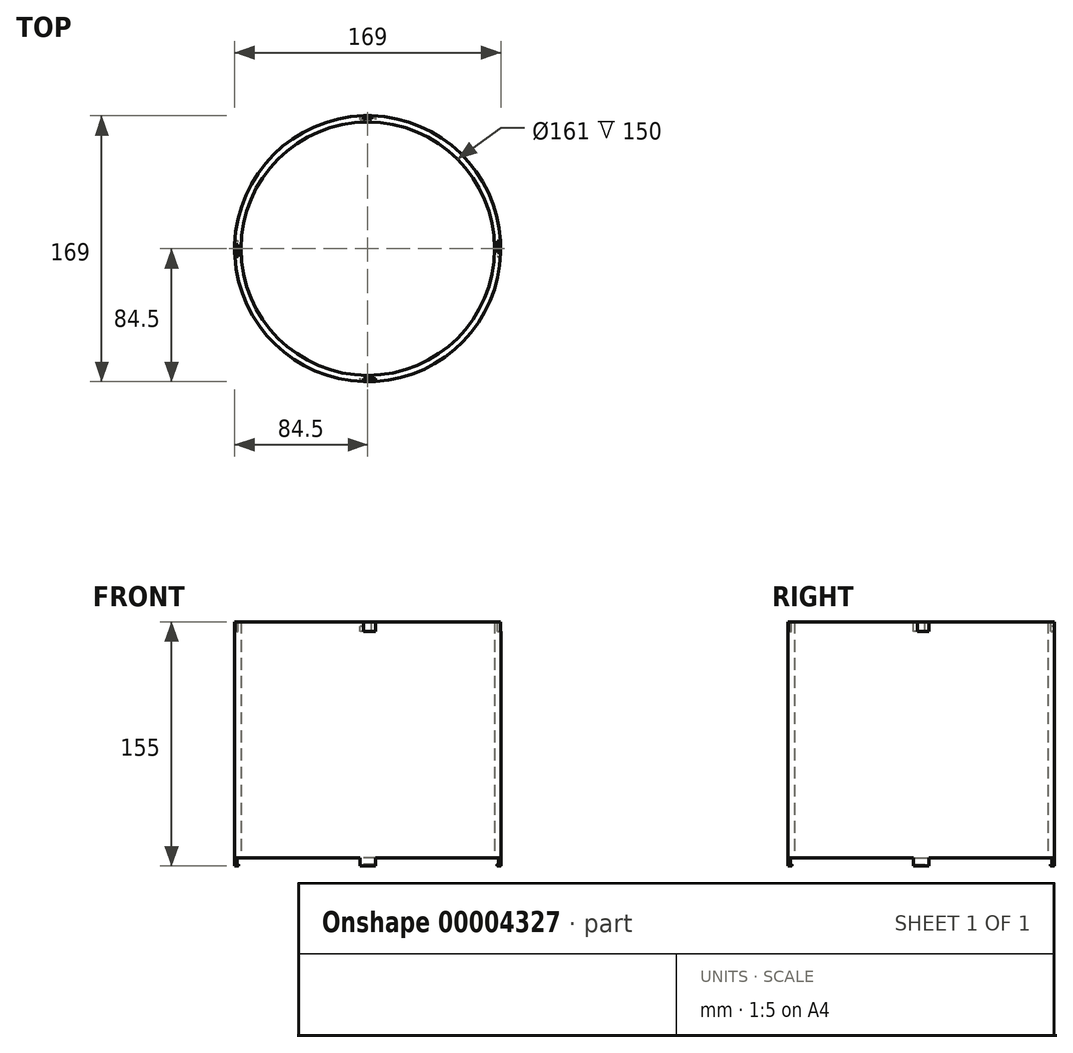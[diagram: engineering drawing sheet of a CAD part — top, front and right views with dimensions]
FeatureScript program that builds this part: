
annotation { "Feature Type Name" : "Feature", "Feature Type Description" : "" }
export const myFeature = defineFeature(function(context is Context, id is Id, definition is map)
    precondition{}
    {
        {
            var Q0;
            Q0=qCreatedBy(makeId("Top.planeOp"),FACE);
            var sketch = newSketch(context, id + "F0", { "sketchPlane" : qUnion([Q0])});
            skCircle(sketch, "E0", {"center": v(0, 0) * mm, "radius": 90 * mm});
            skSolve(sketch);
        }
        {
            var Q0;
            Q0=makeQuery(id+"F0.imprint","IMPRINT",FACE,{"disambiguationData":[TD([[makeQuery(id+"F0.imprint","IMPRINT",EDGE,{"derivedFrom":sQuery(id+"F0.wireOp",EDGE,"E0")}),1.0]])]});
            extrude(context, id + "F1", {"entities" : qUnion([Q0]), "oppositeDirection" : true, "depth" : 150 * mm});
        }
        {
            var Q0;
            Q0=makeQuery(id+"F1.opExtrude","CAP_FACE",FACE,{"disambiguationData":[OSD([sQuery(id+"F0.wireOp",EDGE,"E0")])],"isStart":true});
            var sketch = newSketch(context, id + "F2", { "sketchPlane" : qUnion([Q0])});
            skCircle(sketch, "E1.0", {"center": v(0, 0) * mm, "radius": 80 * mm});
            skSolve(sketch);
        }
        {
            var Q0;
            Q0=makeQuery(id+"F2.imprint","IMPRINT",FACE,{"disambiguationData":[TD([[makeQuery(id+"F2.imprint","IMPRINT",EDGE,{"derivedFrom":sQuery(id+"F2.wireOp",EDGE,"E1.0")}),1.0]])]});
            extrude(context, id + "F3", {"entities" : qUnion([Q0]), "operationType" : NewBodyOperationType.REMOVE, "oppositeDirection" : true, "depth" : 100 * mm});
        }
        {
            var Q0;
            Q0=makeQuery(id+"F1.opExtrude","CAP_FACE",FACE,{"disambiguationData":[OSD([sQuery(id+"F0.wireOp",EDGE,"E0")])],"isStart":true});
            var sketch = newSketch(context, id + "F4", { "sketchPlane" : qUnion([Q0])});
            skCircle(sketch, "E2.0", {"center": v(0, 0) * mm, "radius": 84.5 * mm});
            skSolve(sketch);
        }
        {
            var Q0;
            Q0=makeQuery(id+"F4.imprint","IMPRINT",FACE,{"disambiguationData":[TD([[makeQuery(id+"F4.imprint","IMPRINT",EDGE,{"derivedFrom":sQuery(id+"F4.wireOp",EDGE,"E2.0")}),-1.0]])]});
            extrude(context, id + "F5", {"entities" : qUnion([Q0]), "operationType" : NewBodyOperationType.REMOVE, "oppositeDirection" : true, "depth" : 150 * mm});
        }
        {
            var Q0;
            Q0=makeQuery(id+"F1.opExtrude","CAP_FACE",FACE,{"disambiguationData":[OSD([sQuery(id+"F0.wireOp",EDGE,"E0")])],"isStart":false});
            var sketch = newSketch(context, id + "F6", { "sketchPlane" : qUnion([Q0])});
            skCircle(sketch, "E3.0", {"center": v(0, 0) * mm, "radius": 80.5 * mm});
            skSolve(sketch);
        }
        {
            var Q0;
            Q0=makeQuery(id+"F6.imprint","IMPRINT",FACE,{"disambiguationData":[TD([[makeQuery(id+"F6.imprint","IMPRINT",EDGE,{"derivedFrom":sQuery(id+"F6.wireOp",EDGE,"E3.0")}),1.0]])]});
            extrude(context, id + "F7", {"entities" : qUnion([Q0]), "operationType" : NewBodyOperationType.REMOVE, "oppositeDirection" : true, "depth" : 179.6 * mm});
        }
        {
            var Q0;
            Q0=makeQuery(id+"F1.opExtrude","CAP_FACE",FACE,{"disambiguationData":[OSD([sQuery(id+"F0.wireOp",EDGE,"E0")])],"isStart":false});
            var sketch = newSketch(context, id + "F8", { "sketchPlane" : qUnion([Q0])});
            skLineSegment(sketch, "E4.0", {"start": v(-85, 0) * mm, "end": v(-85, 5) * mm});
            skLineSegment(sketch, "E4.1", {"start": v(-85, 0) * mm, "end": v(-85, -5) * mm});
            skLineSegment(sketch, "E5.0", {"start": v(-83, 0) * mm, "end": v(-83, -5) * mm});
            skLineSegment(sketch, "E5.1", {"start": v(-83, 0) * mm, "end": v(-83, 5) * mm});
            skLineSegment(sketch, "E6", {"start": v(-85, 5) * mm, "end": v(-82.9, 5) * mm});
            skLineSegment(sketch, "E7", {"start": v(-85, -5) * mm, "end": v(-82.9, -5) * mm});
            skLineSegment(sketch, "E8.0", {"start": v(0, -83) * mm, "end": v(5, -83) * mm});
            skLineSegment(sketch, "E8.1", {"start": v(0, -83) * mm, "end": v(-5, -83) * mm});
            skLineSegment(sketch, "E9.0", {"start": v(0, -85) * mm, "end": v(5, -85) * mm});
            skLineSegment(sketch, "E9.1", {"start": v(0, -85) * mm, "end": v(-5, -85) * mm});
            skLineSegment(sketch, "E10", {"start": v(-5, -83) * mm, "end": v(-5, -85) * mm});
            skLineSegment(sketch, "E11", {"start": v(5, -85) * mm, "end": v(5, -83) * mm});
            skLineSegment(sketch, "E12.0", {"start": v(83, 0) * mm, "end": v(83, -5) * mm});
            skLineSegment(sketch, "E12.1", {"start": v(83, 0) * mm, "end": v(83, 5) * mm});
            skLineSegment(sketch, "E13.0", {"start": v(85, 0) * mm, "end": v(85, 5) * mm});
            skLineSegment(sketch, "E13.1", {"start": v(85, 0) * mm, "end": v(85, -5) * mm});
            skLineSegment(sketch, "E14", {"start": v(83, 5) * mm, "end": v(85, 5) * mm});
            skLineSegment(sketch, "E15", {"start": v(85, -5) * mm, "end": v(83, -5) * mm});
            skLineSegment(sketch, "E16.0", {"start": v(0, 85) * mm, "end": v(-5, 85) * mm});
            skLineSegment(sketch, "E16.1", {"start": v(0, 85) * mm, "end": v(5, 85) * mm});
            skLineSegment(sketch, "E17.0", {"start": v(0, 83) * mm, "end": v(5, 83) * mm});
            skLineSegment(sketch, "E17.1", {"start": v(0, 83) * mm, "end": v(-5, 83) * mm});
            skLineSegment(sketch, "E18", {"start": v(-5, 85) * mm, "end": v(-5, 83) * mm});
            skLineSegment(sketch, "E19", {"start": v(5, 85) * mm, "end": v(5, 83) * mm});
            skCircle(sketch, "E20.0", {"center": v(0, 0) * mm, "radius": 84.5 * mm});
            skSolve(sketch);
        }
        {
            var Q0;
            {var subQ3=sQuery(id+"F8.wireOp",EDGE,"E5.0");var subQ6=sQuery(id+"F8.wireOp",EDGE,"E7");var subQ10=makeQuery(id+"F8.imprint","INTERSECT",VERTEX,{"derivedFrom":[subQ3,subQ6]});Q0=makeQuery(id+"F8.imprint","IMPRINT",FACE,{"disambiguationData":[TD([[makeQuery(id+"F8.imprint","IMPRINT",EDGE,{"disambiguationData":[TD([[subQ10,1.0]])],"derivedFrom":subQ3}),-1.0]])]});}
            var Q1;
            {var subQ3=sQuery(id+"F8.wireOp",EDGE,"E8.0");var subQ5=sQuery(id+"F8.wireOp",EDGE,"E11");var subQ8=makeQuery(id+"F8.imprint","INTERSECT",VERTEX,{"derivedFrom":[subQ3,subQ5]});Q1=makeQuery(id+"F8.imprint","IMPRINT",FACE,{"disambiguationData":[TD([[makeQuery(id+"F8.imprint","IMPRINT",EDGE,{"disambiguationData":[TD([[subQ8,1.0]])],"derivedFrom":subQ3}),-1.0]])]});}
            var Q2;
            {var subQ3=sQuery(id+"F8.wireOp",EDGE,"E12.0");var subQ6=sQuery(id+"F8.wireOp",EDGE,"E15");var subQ10=makeQuery(id+"F8.imprint","INTERSECT",VERTEX,{"derivedFrom":[subQ3,subQ6]});Q2=makeQuery(id+"F8.imprint","IMPRINT",FACE,{"disambiguationData":[TD([[makeQuery(id+"F8.imprint","IMPRINT",EDGE,{"disambiguationData":[TD([[subQ10,1.0]])],"derivedFrom":subQ3}),1.0]])]});}
            var Q3;
            {var subQ1=sQuery(id+"F8.wireOp",EDGE,"E19");var subQ5=sQuery(id+"F8.wireOp",EDGE,"E17.0");var subQ6=makeQuery(id+"F8.imprint","INTERSECT",VERTEX,{"derivedFrom":[subQ5,subQ1]});Q3=makeQuery(id+"F8.imprint","IMPRINT",FACE,{"disambiguationData":[TD([[makeQuery(id+"F8.imprint","IMPRINT",EDGE,{"disambiguationData":[TD([[subQ6,1.0]])],"derivedFrom":subQ5}),1.0]])]});}
            extrude(context, id + "F9", {"entities" : qUnion([Q0, Q1, Q2, Q3]), "operationType" : NewBodyOperationType.ADD, "depth" : 5 * mm});
        }
        {
            var Q0;
            Q0=makeQuery(id+"F9.opExtrude","SWEPT_FACE",FACE,{"disambiguationData":[OSD([sQuery(id+"F8.wireOp",EDGE,"E12.0"),sQuery(id+"F8.wireOp",EDGE,"E12.1")])]});
            var sketch = newSketch(context, id + "F10", { "sketchPlane" : qUnion([Q0])});
            skLineSegment(sketch, "E21.0", {"start": v(-5, -154) * mm, "end": v(5, -154) * mm});
            skSolve(sketch);
        }
        {
            var Q0;
            Q0=makeQuery(id+"F9.opExtrude","SWEPT_FACE",FACE,{"disambiguationData":[OSD([sQuery(id+"F8.wireOp",EDGE,"E17.0"),sQuery(id+"F8.wireOp",EDGE,"E17.1")])]});
            var sketch = newSketch(context, id + "F11", { "sketchPlane" : qUnion([Q0])});
            skLineSegment(sketch, "E22.0", {"start": v(-5, -154) * mm, "end": v(5, -154) * mm});
            skSolve(sketch);
        }
        {
            var Q0;
            Q0=makeQuery(id+"F9.opExtrude","SWEPT_FACE",FACE,{"disambiguationData":[OSD([sQuery(id+"F8.wireOp",EDGE,"E5.0"),sQuery(id+"F8.wireOp",EDGE,"E5.1")])]});
            var sketch = newSketch(context, id + "F12", { "sketchPlane" : qUnion([Q0])});
            skLineSegment(sketch, "E23.0", {"start": v(-5, -154) * mm, "end": v(5, -154) * mm});
            skSolve(sketch);
        }
        {
            var Q0;
            Q0=makeQuery(id+"F9.opExtrude","SWEPT_FACE",FACE,{"disambiguationData":[OSD([sQuery(id+"F8.wireOp",EDGE,"E8.0"),sQuery(id+"F8.wireOp",EDGE,"E8.1")])]});
            var sketch = newSketch(context, id + "F13", { "sketchPlane" : qUnion([Q0])});
            skLineSegment(sketch, "E24.0", {"start": v(-5, -154) * mm, "end": v(5, -154) * mm});
            skSolve(sketch);
        }
        {
            var Q0;
            {var subQ2=sQuery(id+"F13.wireOp",EDGE,"E24.0");Q0=makeQuery(id+"F13.imprint","IMPRINT",FACE,{"disambiguationData":[TD([[makeQuery(id+"F13.imprint","IMPRINT",EDGE,{"derivedFrom":subQ2}),-1.0]])]});}
            extrude(context, id + "F14", {"entities" : qUnion([Q0]), "operationType" : NewBodyOperationType.ADD, "depth" : 1 * mm});
        }
        {
            var Q0;
            {var subQ2=sQuery(id+"F10.wireOp",EDGE,"E21.0");Q0=makeQuery(id+"F10.imprint","IMPRINT",FACE,{"disambiguationData":[TD([[makeQuery(id+"F10.imprint","IMPRINT",EDGE,{"derivedFrom":subQ2}),-1.0]])]});}
            extrude(context, id + "F15", {"entities" : qUnion([Q0]), "operationType" : NewBodyOperationType.ADD, "depth" : 1 * mm});
        }
        {
            var Q0;
            {var subQ2=sQuery(id+"F11.wireOp",EDGE,"E22.0");Q0=makeQuery(id+"F11.imprint","IMPRINT",FACE,{"disambiguationData":[TD([[makeQuery(id+"F11.imprint","IMPRINT",EDGE,{"derivedFrom":subQ2}),-1.0]])]});}
            extrude(context, id + "F16", {"entities" : qUnion([Q0]), "operationType" : NewBodyOperationType.ADD, "depth" : 1 * mm});
        }
        {
            var Q0;
            {var subQ2=sQuery(id+"F12.wireOp",EDGE,"E23.0");Q0=makeQuery(id+"F12.imprint","IMPRINT",FACE,{"disambiguationData":[TD([[makeQuery(id+"F12.imprint","IMPRINT",EDGE,{"derivedFrom":subQ2}),-1.0]])]});}
            extrude(context, id + "F17", {"entities" : qUnion([Q0]), "operationType" : NewBodyOperationType.ADD, "depth" : 1 * mm});
        }
        {
            var Q0;
            Q0=makeQuery(id+"F17.opExtrude","CAP_EDGE",EDGE,{"disambiguationData":[OSD([sQuery(id+"F8.wireOp",EDGE,"E5.0"),sQuery(id+"F8.wireOp",EDGE,"E5.1")])],"isStart":false});
            var Q1;
            Q1=makeQuery(id+"F17.opExtrude","CAP_EDGE",EDGE,{"disambiguationData":[OSD([sQuery(id+"F12.wireOp",EDGE,"E23.0")])],"isStart":false});
            fillet(context, id + "F18", {"entities" : qUnion([Q0, Q1]), "radius" : 0.5 * mm, "tangentPropagation" : true, "allowEdgeOverflow" : false});
        }
        {
            var Q0;
            Q0=makeQuery(id+"F14.opExtrude","CAP_EDGE",EDGE,{"disambiguationData":[OSD([sQuery(id+"F13.wireOp",EDGE,"a1c1dbc0-bdf1-4701-884e-e09ee9ca7c5f.0")])],"isStart":false});
            var Q1;
            Q1=makeQuery(id+"F14.opExtrude","CAP_EDGE",EDGE,{"disambiguationData":[OSD([sQuery(id+"F8.wireOp",EDGE,"E8.0"),sQuery(id+"F8.wireOp",EDGE,"E8.1")])],"isStart":false});
            fillet(context, id + "F19", {"entities" : qUnion([Q0, Q1]), "radius" : 0.5 * mm, "tangentPropagation" : true, "allowEdgeOverflow" : false});
        }
        {
            var Q0;
            Q0=makeQuery(id+"F15.opExtrude","CAP_EDGE",EDGE,{"disambiguationData":[OSD([sQuery(id+"F8.wireOp",EDGE,"E12.0"),sQuery(id+"F8.wireOp",EDGE,"E12.1")])],"isStart":false});
            var Q1;
            Q1=makeQuery(id+"F15.opExtrude","CAP_EDGE",EDGE,{"disambiguationData":[OSD([sQuery(id+"F10.wireOp",EDGE,"E21.0")])],"isStart":false});
            fillet(context, id + "F20", {"entities" : qUnion([Q0, Q1]), "radius" : 0.5 * mm, "tangentPropagation" : true, "allowEdgeOverflow" : false});
        }
        {
            var Q0;
            Q0=makeQuery(id+"F16.opExtrude","CAP_EDGE",EDGE,{"disambiguationData":[OSD([sQuery(id+"F8.wireOp",EDGE,"E17.0"),sQuery(id+"F8.wireOp",EDGE,"E17.1")])],"isStart":false});
            var Q1;
            Q1=makeQuery(id+"F16.opExtrude","CAP_EDGE",EDGE,{"disambiguationData":[OSD([sQuery(id+"F11.wireOp",EDGE,"E22.0")])],"isStart":false});
            fillet(context, id + "F21", {"entities" : qUnion([Q0, Q1]), "radius" : 0.5 * mm, "tangentPropagation" : true, "allowEdgeOverflow" : false});
        }
        {
            var Q0;
            Q0=makeQuery(id+"F4.imprint","IMPRINT",FACE,{"disambiguationData":[TD([[makeQuery(id+"F4.imprint","IMPRINT",EDGE,{"derivedFrom":sQuery(id+"F4.wireOp",EDGE,"E2.0")}),1.0]])]});
            var sketch = newSketch(context, id + "F22", { "sketchPlane" : qUnion([Q0])});
            skCircle(sketch, "E25.0", {"center": v(0, 0) * mm, "radius": 84.5 * mm});
            skCircle(sketch, "E26.0", {"center": v(0, 0) * mm, "radius": 80 * mm});
            skLineSegment(sketch, "E27", {"start": v(-84.5, 2.5) * mm, "end": v(-81.5, 2.5) * mm});
            skLineSegment(sketch, "E28", {"start": v(-84.5, -2.5) * mm, "end": v(-84.46, -2.5) * mm});
            skLineSegment(sketch, "E29", {"start": v(2.5, 81.81) * mm, "end": v(2.5, 84.5) * mm});
            skLineSegment(sketch, "E30", {"start": v(81.3, -2.5) * mm, "end": v(84.5, -2.5) * mm});
            skLineSegment(sketch, "E31", {"start": v(-2.5, -84.5) * mm, "end": v(-2.5, -82.5) * mm});
            skLineSegment(sketch, "E32", {"start": v(-2.5, -84.5) * mm, "end": v(-2.5, -81.7) * mm});
            skLineSegment(sketch, "E33.0", {"start": v(5, -81.52) * mm, "end": v(5, -84.5) * mm});
            skLineSegment(sketch, "E34.0", {"start": v(81.4, 5) * mm, "end": v(84.5, 5) * mm});
            skLineSegment(sketch, "E35.0", {"start": v(-5, 84.5) * mm, "end": v(-5, 81.47) * mm});
            skLineSegment(sketch, "E36.0", {"start": v(-84.5, -5) * mm, "end": v(-80.8, -5) * mm});
            skCircle(sketch, "E37.0", {"center": v(0, 0) * mm, "radius": 82.5 * mm});
            skSolve(sketch);
        }
        {
            var Q0;
            {var subQ5=sQuery(id+"F22.wireOp",EDGE,"E25.0");var subQ7=makeQuery(id+"F22.imprint","IMPRINT",VERTEX,{"derivedFrom":subQ5});Q0=makeQuery(id+"F22.imprint","IMPRINT",FACE,{"disambiguationData":[TD([[makeQuery(id+"F22.imprint","IMPRINT",EDGE,{"disambiguationData":[TD([[subQ7,1.0]])],"derivedFrom":subQ5}),1.0]])]});}
            var Q1;
            {var subQ3=sQuery(id+"F22.wireOp",EDGE,"E32");var subQ8=makeQuery(id+"F22.imprint","IMPRINT",VERTEX,{"derivedFrom":subQ3});Q1=makeQuery(id+"F22.imprint","IMPRINT",FACE,{"disambiguationData":[TD([[makeQuery(id+"F22.imprint","IMPRINT",EDGE,{"disambiguationData":[TD([[subQ8,1.0]])],"derivedFrom":subQ3}),-1.0]])]});}
            var Q2;
            {var subQ3=sQuery(id+"F22.wireOp",EDGE,"E30");var subQ5=sQuery(id+"F22.wireOp",EDGE,"E25.0");var subQ7=makeQuery(id+"F22.imprint","INTERSECT",VERTEX,{"derivedFrom":[subQ3,subQ5]});Q2=makeQuery(id+"F22.imprint","IMPRINT",FACE,{"disambiguationData":[TD([[makeQuery(id+"F22.imprint","IMPRINT",EDGE,{"disambiguationData":[TD([[subQ7,1.0]])],"derivedFrom":subQ3}),1.0]])]});}
            var Q3;
            {var subQ0=sQuery(id+"F22.wireOp",EDGE,"E25.0");var subQ3=sQuery(id+"F22.wireOp",EDGE,"E29");var subQ4=makeQuery(id+"F22.imprint","INTERSECT",VERTEX,{"derivedFrom":[subQ3,subQ0]});Q3=makeQuery(id+"F22.imprint","IMPRINT",FACE,{"disambiguationData":[TD([[makeQuery(id+"F22.imprint","IMPRINT",EDGE,{"disambiguationData":[TD([[subQ4,1.0]])],"derivedFrom":subQ3}),1.0]])]});}
            extrude(context, id + "F23", {"entities" : qUnion([Q0, Q1, Q2, Q3]), "operationType" : NewBodyOperationType.REMOVE, "oppositeDirection" : true, "depth" : 6 * mm});
        }
        {
            var Q0;
            Q0=makeQuery(id+"F1.opExtrude","CAP_FACE",FACE,{"disambiguationData":[OSD([sQuery(id+"F0.wireOp",EDGE,"E0")])],"isStart":true});
            var sketch = newSketch(context, id + "F24", { "sketchPlane" : qUnion([Q0])});
            skLineSegment(sketch, "E38", {"start": v(5, -84.35) * mm, "end": v(5, -84.35) * mm});
            skLineSegment(sketch, "E39.0", {"start": v(2.5, -84.35) * mm, "end": v(2.5, -84.35) * mm});
            skLineSegment(sketch, "E40.0", {"start": v(84.35, 2.5) * mm, "end": v(84.35, 2.5) * mm});
            skLineSegment(sketch, "E41", {"start": v(84.35, 5) * mm, "end": v(84.35, 5) * mm});
            skLineSegment(sketch, "E42.0", {"start": v(-2.5, 84.35) * mm, "end": v(-2.5, 84.35) * mm});
            skLineSegment(sketch, "E43", {"start": v(-5, 84.35) * mm, "end": v(-5, 84.35) * mm});
            skLineSegment(sketch, "E44.0", {"start": v(-84.35, -2.5) * mm, "end": v(-84.35, -2.5) * mm});
            skLineSegment(sketch, "E45", {"start": v(-84.35, -5) * mm, "end": v(-84.35, -5) * mm});
            skArc(sketch, "E46.0", {"start": v(2.56, 84.46) * mm, "mid": v(-1.28, 84.5) * mm, "end": v(-5.12, 84.34) * mm});
            skLineSegment(sketch, "E47.0", {"start": v(-2.5, 85.02) * mm, "end": v(-2.5, 82.35) * mm});
            skArc(sketch, "E48.0", {"start": v(2.5, 82.46) * mm, "mid": v(-1.25, 82.5) * mm, "end": v(-5, 82.35) * mm});
            skLineSegment(sketch, "E49", {"start": v(-5, 82.35) * mm, "end": v(-5, 84.35) * mm});
            skArc(sketch, "E50.0", {"start": v(-84.46, 2.56) * mm, "mid": v(-84.5, -1.28) * mm, "end": v(-84.34, -5.12) * mm});
            skLineSegment(sketch, "E51.0", {"start": v(-88.37, -2.5) * mm, "end": v(-82.35, -2.5) * mm});
            skArc(sketch, "E52.0", {"start": v(-82.46, 2.5) * mm, "mid": v(-82.5, -1.25) * mm, "end": v(-82.35, -5) * mm});
            skArc(sketch, "E53.0", {"start": v(-2.56, -84.46) * mm, "mid": v(1.28, -84.5) * mm, "end": v(5.12, -84.34) * mm});
            skArc(sketch, "E54.0", {"start": v(-2.5, -82.46) * mm, "mid": v(1.25, -82.5) * mm, "end": v(5, -82.35) * mm});
            skLineSegment(sketch, "E55.0", {"start": v(2.5, -82.35) * mm, "end": v(2.5, -87.42) * mm});
            skArc(sketch, "E56.0", {"start": v(84.46, -2.56) * mm, "mid": v(84.5, 1.28) * mm, "end": v(84.34, 5.12) * mm});
            skArc(sketch, "E57.0", {"start": v(82.46, -2.5) * mm, "mid": v(82.5, 1.25) * mm, "end": v(82.35, 5) * mm});
            skLineSegment(sketch, "E58.0", {"start": v(82.35, 2.5) * mm, "end": v(85.22, 2.5) * mm});
            skSolve(sketch);
        }
        {
            var Q0;
            {var subQ0=makeQuery(id+"F23.boolean.opBoolean","COPY",EDGE,{"derivedFrom":makeQuery(id+"F23.opExtrude","CAP_EDGE",EDGE,{"disambiguationData":[OSD([sQuery(id+"F22.wireOp",EDGE,"E33.0")])],"isStart":true})});Q0=makeQuery(id+"F24.imprint","IMPRINT",FACE,{"disambiguationData":[TD([[makeQuery(id+"F24.imprint","IMPRINT",EDGE,{"derivedFrom":subQ0}),-1.0]])]});}
            var Q1;
            {var subQ0=makeQuery(id+"F23.boolean.opBoolean","COPY",EDGE,{"derivedFrom":makeQuery(id+"F23.opExtrude","CAP_EDGE",EDGE,{"disambiguationData":[OSD([sQuery(id+"F22.wireOp",EDGE,"E34.0")])],"isStart":true})});Q1=makeQuery(id+"F24.imprint","IMPRINT",FACE,{"disambiguationData":[TD([[makeQuery(id+"F24.imprint","IMPRINT",EDGE,{"derivedFrom":subQ0}),-1.0]])]});}
            var Q2;
            {var subQ0=sQuery(id+"F24.wireOp",EDGE,"E49");Q2=makeQuery(id+"F24.imprint","IMPRINT",FACE,{"disambiguationData":[TD([[makeQuery(id+"F24.imprint","IMPRINT",EDGE,{"derivedFrom":subQ0}),1.0]])]});}
            var Q3;
            {var subQ0=makeQuery(id+"F23.boolean.opBoolean","COPY",EDGE,{"derivedFrom":makeQuery(id+"F23.opExtrude","CAP_EDGE",EDGE,{"disambiguationData":[OSD([sQuery(id+"F22.wireOp",EDGE,"E36.0")])],"isStart":true})});Q3=makeQuery(id+"F24.imprint","IMPRINT",FACE,{"disambiguationData":[TD([[makeQuery(id+"F24.imprint","IMPRINT",EDGE,{"derivedFrom":subQ0}),1.0]])]});}
            extrude(context, id + "F25", {"entities" : qUnion([Q0, Q1, Q2, Q3]), "operationType" : NewBodyOperationType.ADD, "oppositeDirection" : true, "depth" : 3 * mm});
        }
    });
